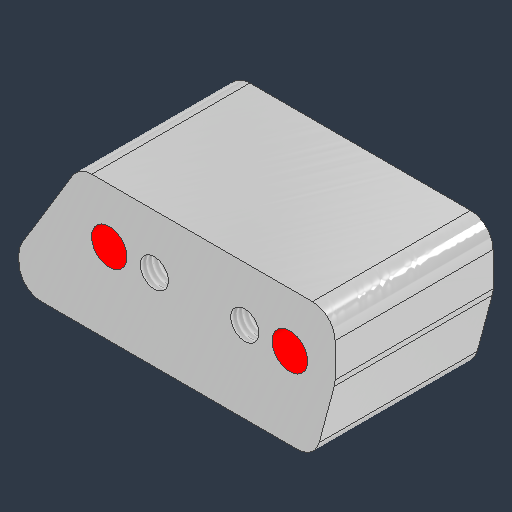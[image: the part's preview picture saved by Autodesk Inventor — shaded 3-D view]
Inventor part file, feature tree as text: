
AUTODESK INVENTOR PART (.ipt)
format: ipt  version: 2024.3 (Build 283343000, 343)  size: 211,456 bytes
history: native  units: in
note: dims shown in document units (in); Inventor stores cm internally (conversion verified against a paired STEP export)
features: sketch x4, hole x3, chamfer x2, extrude x1, fillet x1
ambient origin geometry x8: Origin, YZ Plane, XZ Plane, XY Plane, X Axis, Y Axis, Z Axis, Center Point
bodies: Solid1 (feature_tree)
feature tree (11):
  extrude  "Extrusion1"  Depth=1.75in
  hole  "Hole1"  [1 undecoded]
  hole  "Hole2"  [1 undecoded]
  hole  "Hole4"  [1 undecoded]
  chamfer  "Chamfer2"  Distance=1.0in
  chamfer  "Chamfer3"  Distance=0.125in Angle=15.0deg
  fillet  "Fillet1"  Radius=0.125in
  sketch  "Sketch1"  dims[d0=0.75in d1=1.75in]
  sketch  "Sketch3"  dims[d2=0.875in d3=0.0in d35=1.0in]
  sketch  "Sketch4"  dims[d36=0.197in d37=0.38in d38=0.256in d39=0.19in d40=90.0deg d41=1.0in d42=0.8108in d43=0.5in]
  sketch  "Sketch6"  dims[d44=0.156in d45=0.38in d46=0.385in d47=0.25in d48=0.5635in d49=1.0in d50=0.8108in d51=0.125in d56=1.0in d58=0.42in d59=0.125in d60=15.0deg d61=0.55in d62=0.125in d63=0.2145in d80=1.9685in d82=0.3937in d83=0.75in d84=0.25in d85=1.0in d86=0.0968in d87=0.236in d88=0.375in d89=0.25in d90=0.5635in d91=0.346in d92=0.8108in d93=0.45in]
note: 3 required parameter values undecoded (feature->parameter linkage not recoverable at this tier; creation-order binding heuristic only, values carry confidence <= 0.55)
